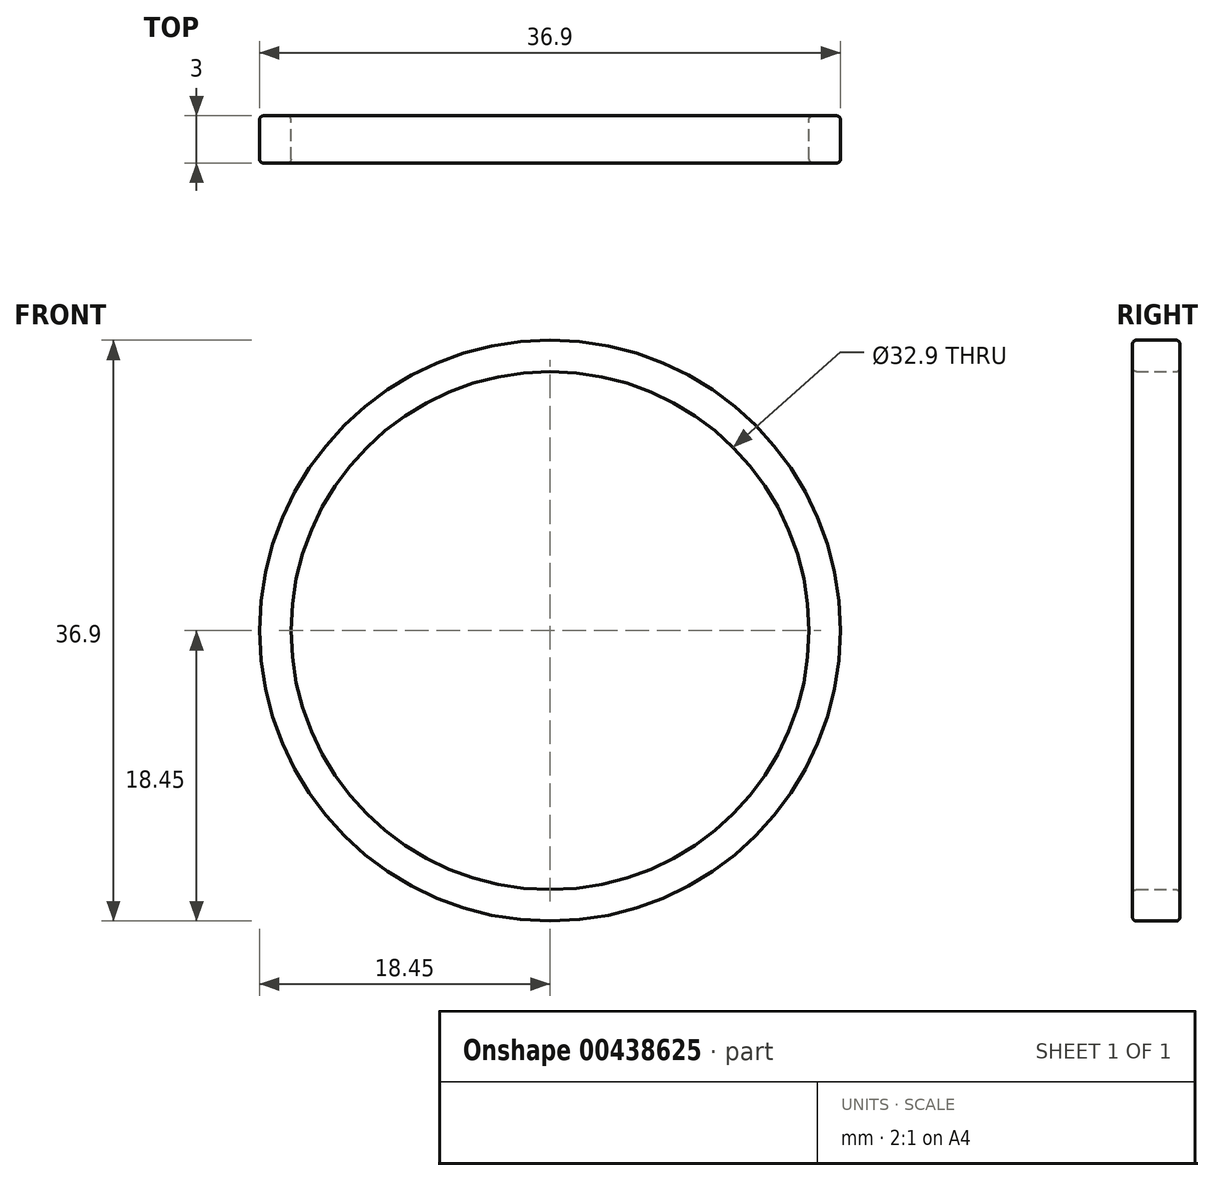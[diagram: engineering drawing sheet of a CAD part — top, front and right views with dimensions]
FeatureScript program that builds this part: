
annotation { "Feature Type Name" : "Feature", "Feature Type Description" : "" }
export const myFeature = defineFeature(function(context is Context, id is Id, definition is map)
    precondition{}
    {
        {
            var Q0;
            Q0=qCreatedBy(makeId("Front.planeOp"),FACE);
            var sketch = newSketch(context, id + "F0", { "sketchPlane" : qUnion([Q0])});
            skCircle(sketch, "E0", {"center": v(0, 0) * mm, "radius": 16.45 * mm});
            skCircle(sketch, "E1.0", {"center": v(0, 0) * mm, "radius": 18.45 * mm});
            skSolve(sketch);
        }
        {
            var Q0;
            Q0=makeQuery(id+"F0.imprint","IMPRINT",FACE,{"disambiguationData":[TD([[makeQuery(id+"F0.imprint","IMPRINT",EDGE,{"derivedFrom":sQuery(id+"F0.wireOp",EDGE,"E0")}),-1.0]])]});
            extrude(context, id + "F1", {"entities" : qUnion([Q0]), "endBound" : BoundingType.SYMMETRIC, "depth" : 3 * mm});
        }
        {
            var Q0;
            Q0=makeQuery(id+"F1.opExtrude","CAP_EDGE",EDGE,{"disambiguationData":[OSD([sQuery(id+"F0.wireOp",EDGE,"E0")])],"isStart":false});
            fillet(context, id + "F2", {"entities" : qUnion([Q0]), "radius" : .25 * mm, "tangentPropagation" : true, "allowEdgeOverflow" : false});
        }
        {
            var Q0;
            Q0=makeQuery(id+"F1.opExtrude","CAP_EDGE",EDGE,{"disambiguationData":[OSD([sQuery(id+"F0.wireOp",EDGE,"E0")])],"isStart":true});
            fillet(context, id + "F3", {"entities" : qUnion([Q0]), "radius" : .25 * mm, "tangentPropagation" : true, "allowEdgeOverflow" : false});
        }
        {
            var Q0;
            Q0=makeQuery(id+"F1.opExtrude","CAP_EDGE",EDGE,{"disambiguationData":[OSD([sQuery(id+"F0.wireOp",EDGE,"E1.0")])],"isStart":false});
            var Q1;
            Q1=makeQuery(id+"F1.opExtrude","CAP_EDGE",EDGE,{"disambiguationData":[OSD([sQuery(id+"F0.wireOp",EDGE,"E1.0")])],"isStart":true});
            fillet(context, id + "F4", {"entities" : qUnion([Q0, Q1]), "radius" : .25 * mm, "tangentPropagation" : true, "allowEdgeOverflow" : false});
        }
    });
